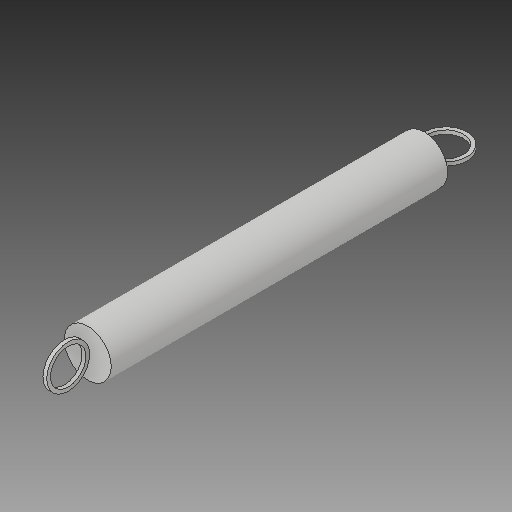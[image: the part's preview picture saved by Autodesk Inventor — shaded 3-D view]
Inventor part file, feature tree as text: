
AUTODESK INVENTOR PART (.ipt)
format: ipt  version: 2018 (Build 220112000, 112)  size: 121,344 bytes
history: native  units: in
note: dims shown in document units (in); Inventor stores cm internally (conversion verified against a paired STEP export)
features: extrude x3, sketch x3
ambient origin geometry x8: Origin, YZ Plane, XZ Plane, XY Plane, X Axis, Y Axis, Z Axis, Center Point
bodies: Solid1 (feature_tree)
feature tree (6):
  extrude  "Extrusion1"  Depth=3.585in TaperAngle=0.0deg
  extrude  "Extrusion2"  Depth=0.2288in
  extrude  "Extrusion3"  Depth=0.04in TaperAngle=0.0deg
  sketch  "Sketch2"  dims[d0=0.5in d1=3.585in d2=0.0in]
  sketch  "Sketch3"  dims[d3=0.2288in d4=0.4575in]
  sketch  "Sketch4"  dims[d5=0.04in d6=0.04in d7=0.0in d8=0.2288in d9=0.4575in d10=0.04in d11=0.04in d12=0.0in]
